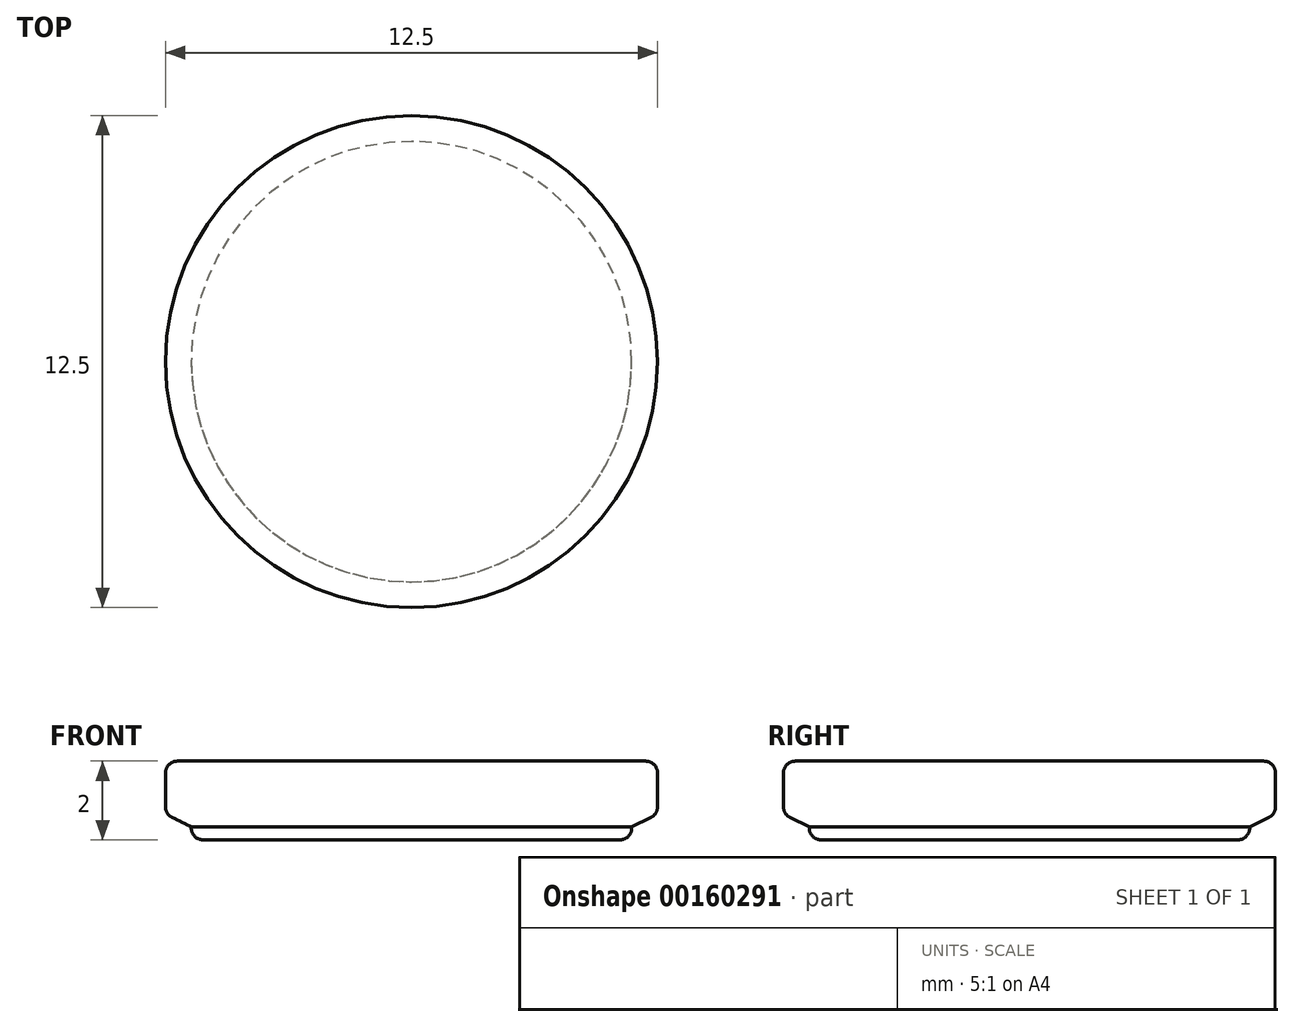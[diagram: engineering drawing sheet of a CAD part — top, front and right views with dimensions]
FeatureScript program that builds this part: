
annotation { "Feature Type Name" : "Feature", "Feature Type Description" : "" }
export const myFeature = defineFeature(function(context is Context, id is Id, definition is map)
    precondition{}
    {
        {
            var Q0;
            Q0=qCreatedBy(makeId("Front.planeOp"),FACE);
            var sketch = newSketch(context, id + "F0", { "sketchPlane" : qUnion([Q0])});
            skLineSegment(sketch, "E0", {"start": v(0, 2) * mm, "end": v(6.25, 2) * mm});
            skLineSegment(sketch, "E1", {"start": v(6.25, 2) * mm, "end": v(6.25, 0.65) * mm});
            skLineSegment(sketch, "E2", {"start": v(6.25, 0.65) * mm, "end": v(5.6, 0.33) * mm});
            skLineSegment(sketch, "E3", {"start": v(5.6, 0.33) * mm, "end": v(5.6, 0) * mm});
            skLineSegment(sketch, "E4", {"start": v(5.6, 0) * mm, "end": v(0, 0) * mm});
            skLineSegment(sketch, "E5", {"start": v(0, 0) * mm, "end": v(0, 2) * mm});
            skSolve(sketch);
        }
        {
            var Q0;
            Q0 = qSketchRegion(id + "F0", true);
            var Q1;
            Q1=sQuery(id+"F0.wireOp",EDGE,"E5");
            revolve(context, id + "F1", {"entities" : qUnion([Q0]), "axis" : qUnion([Q1]), "revolveType" : RevolveType.FULL});
        }
        {
            var Q0;
            Q0=makeQuery(id+"F1.opRevolve","SWEPT_EDGE",EDGE,{"disambiguationData":[OSD([sQuery(id+"F0.wireOp",EDGE,"E0"),sQuery(id+"F0.wireOp",EDGE,"E1")])]});
            var Q1;
            Q1=makeQuery(id+"F1.opRevolve","SWEPT_EDGE",EDGE,{"disambiguationData":[OSD([sQuery(id+"F0.wireOp",EDGE,"E3"),sQuery(id+"F0.wireOp",EDGE,"E4")])]});
            var Q2;
            Q2=makeQuery(id+"F1.opRevolve","SWEPT_EDGE",EDGE,{"disambiguationData":[OSD([sQuery(id+"F0.wireOp",EDGE,"E1"),sQuery(id+"F0.wireOp",EDGE,"E2")])]});
            fillet(context, id + "F2", {"entities" : qUnion([Q0, Q1, Q2]), "radius" : 0.3 * mm, "allowEdgeOverflow" : false});
        }
    });
